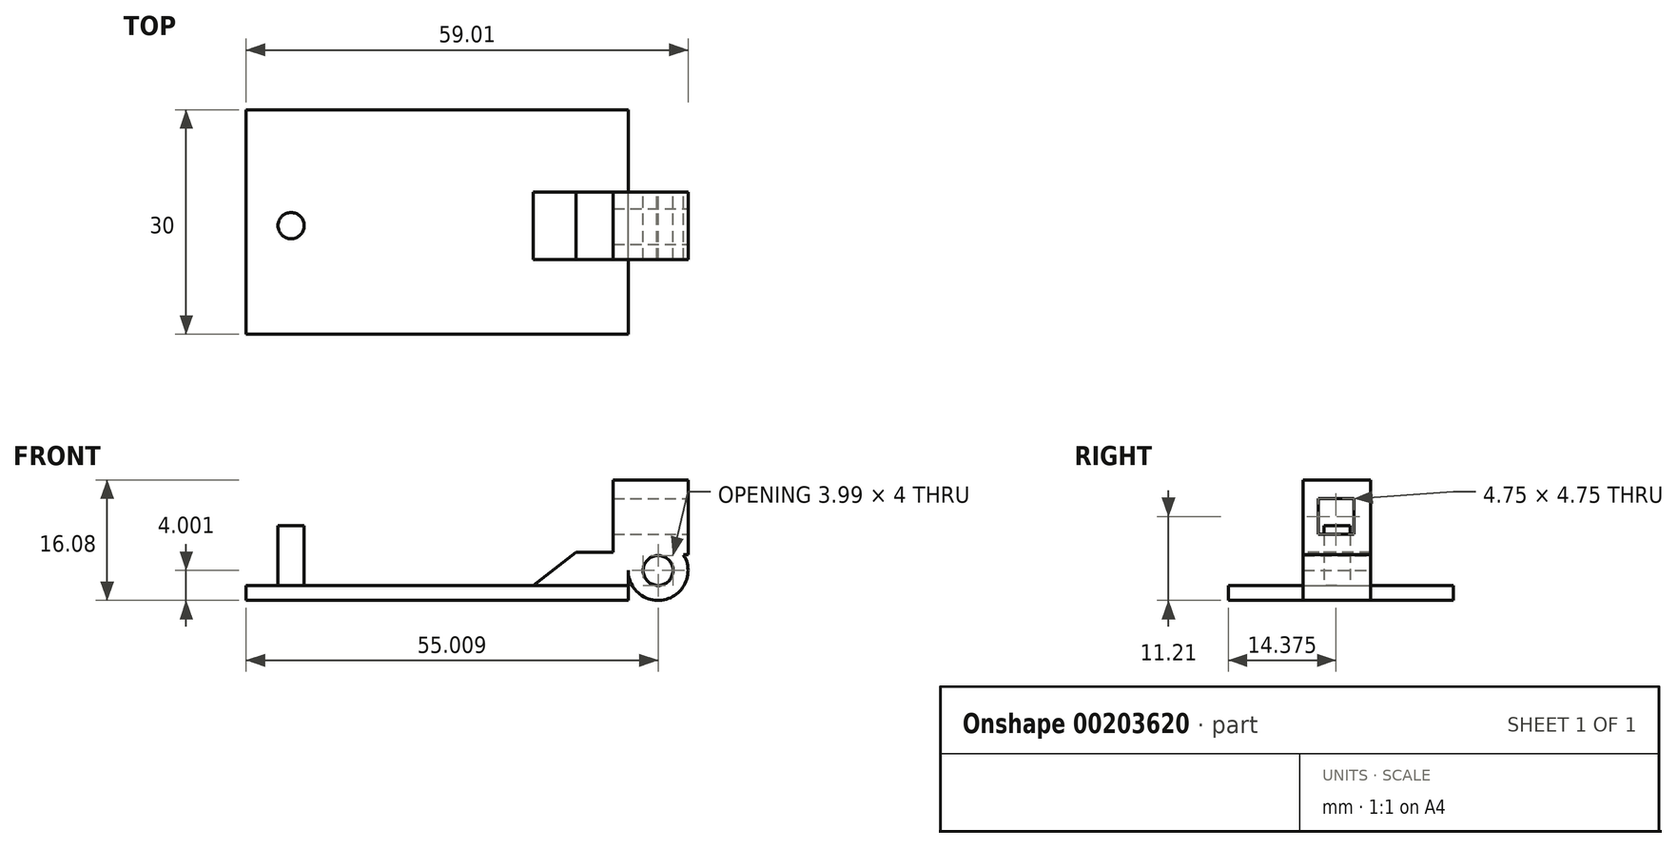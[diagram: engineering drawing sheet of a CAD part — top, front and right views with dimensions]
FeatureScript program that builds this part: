
annotation { "Feature Type Name" : "Feature", "Feature Type Description" : "" }
export const myFeature = defineFeature(function(context is Context, id is Id, definition is map)
    precondition{}
    {
        {
            var Q0;
            Q0=qCreatedBy(makeId("Front.planeOp"),FACE);
            var sketch = newSketch(context, id + "F0", { "sketchPlane" : qUnion([Q0])});
            skLineSegment(sketch, "E0.bottom", {"start": v(0, -4) * mm, "end": v(55, -4) * mm});
            skLineSegment(sketch, "E0.top", {"start": v(0, -2) * mm, "end": v(55, -2) * mm});
            skLineSegment(sketch, "E0.left", {"start": v(0, -4) * mm, "end": v(0, -2) * mm});
            skLineSegment(sketch, "E0.right", {"start": v(55, -4) * mm, "end": v(55, -2) * mm});
            skLineSegment(sketch, "E1", {"start": v(55, -2) * mm, "end": v(55, 0) * mm});
            skCircle(sketch, "E2", {"center": v(55, 0) * mm, "radius": 4 * mm});
            skCircle(sketch, "E3", {"center": v(55, 0) * mm, "radius": 2 * mm});
            skLineSegment(sketch, "E4", {"start": v(51, 0) * mm, "end": v(51, -4) * mm});
            skLineSegment(sketch, "E5", {"start": v(51.84, 2.44) * mm, "end": v(44.02, 2.44) * mm});
            skLineSegment(sketch, "E6", {"start": v(44.02, 2.44) * mm, "end": v(38.32, -2) * mm});
            skSolve(sketch);
        }
        {
            var Q0;
            {var subQ1=sQuery(id+"F0.wireOp",EDGE,"msGZdTGy-w9Bb-bp7U-2m3c-FxzwhI83p8LT");var subQ3=sQuery(id+"F0.wireOp",EDGE,"E0.top");var subQ4=makeQuery(id+"F0.imprint","INTERSECT",VERTEX,{"derivedFrom":[subQ1,subQ3]});Q0=makeQuery(id+"F0.imprint","IMPRINT",FACE,{"disambiguationData":[TD([[makeQuery(id+"F0.imprint","IMPRINT",EDGE,{"disambiguationData":[TD([[subQ4,-1.0]])],"derivedFrom":subQ3}),-1.0]])]});}
            var Q1;
            {var subQ0=sQuery(id+"F0.wireOp",EDGE,"E0.left");Q1=makeQuery(id+"F0.imprint","IMPRINT",FACE,{"disambiguationData":[TD([[makeQuery(id+"F0.imprint","IMPRINT",EDGE,{"derivedFrom":subQ0}),-1.0]])]});}
            var Q2;
            {var subQ0=sQuery(id+"F0.wireOp",EDGE,"E0.right");Q2=makeQuery(id+"F0.imprint","IMPRINT",FACE,{"disambiguationData":[TD([[makeQuery(id+"F0.imprint","IMPRINT",EDGE,{"derivedFrom":subQ0}),1.0]])]});}
            var Q3;
            {var subQ4=sQuery(id+"F0.wireOp",EDGE,"E0.right");var subQ5=sQuery(id+"F0.wireOp",EDGE,"E0.bottom");var subQ6=makeQuery(id+"F0.imprint","INTERSECT",VERTEX,{"derivedFrom":[subQ5,subQ4]});Q3=makeQuery(id+"F0.imprint","IMPRINT",FACE,{"disambiguationData":[TD([[makeQuery(id+"F0.imprint","IMPRINT",EDGE,{"disambiguationData":[TD([[subQ6,1.0]])],"derivedFrom":subQ5}),-1.0]])]});}
            var Q4;
            {var subQ1=sQuery(id+"F0.wireOp",EDGE,"E0.bottom");var subQ5=sQuery(id+"F0.wireOp",EDGE,"E0.right");var subQ6=makeQuery(id+"F0.imprint","INTERSECT",VERTEX,{"derivedFrom":[subQ1,subQ5]});Q4=makeQuery(id+"F0.imprint","IMPRINT",FACE,{"disambiguationData":[TD([[makeQuery(id+"F0.imprint","IMPRINT",EDGE,{"disambiguationData":[TD([[subQ6,1.0]])],"derivedFrom":subQ1}),1.0]])]});}
            var Q5;
            {var subQ6=sQuery(id+"F0.wireOp",EDGE,"E5");Q5=makeQuery(id+"F0.imprint","IMPRINT",FACE,{"disambiguationData":[TD([[makeQuery(id+"F0.imprint","IMPRINT",EDGE,{"derivedFrom":subQ6}),1.0]])]});}
            extrude(context, id + "F1", {"entities" : qUnion([Q0, Q1, Q2, Q3, Q4, Q5]), "depth" : 20 * mm, "hasSecondDirection" : true, "secondDirectionOppositeDirection" : false, "secondDirectionDepth" : 11 * mm});
        }
        {
            var Q0;
            {var subQ0=sQuery(id+"F0.wireOp",EDGE,"E0.bottom");Q0=makeQuery(id+"F0amyIbCvxJC7EA_1.boolean.opBoolean","MERGE",FACE,{"derivedFrom":[makeQuery(id+"FixQ7C7vZYy5nc9_1.boolean.opBoolean","MERGE",FACE,{"derivedFrom":[makeQuery(id+"F1.opExtrude","SWEPT_FACE",FACE,{"disambiguationData":[OSD([subQ0])]}),makeQuery(id+"FixQ7C7vZYy5nc9_1.opExtrude","SWEPT_FACE",FACE,{"disambiguationData":[OSD([subQ0])]})]}),makeQuery(id+"F0amyIbCvxJC7EA_1.opExtrude","SWEPT_FACE",FACE,{"disambiguationData":[OSD([subQ0])]})]});}
            var sketch = newSketch(context, id + "F2", { "sketchPlane" : qUnion([Q0])});
            skLineSegment(sketch, "E7", {"start": v(6, 20) * mm, "end": v(6, 15.5) * mm});
            skCircle(sketch, "E8", {"center": v(6, 15.5) * mm, "radius": 1.75 * mm});
            skSolve(sketch);
        }
        {
            var Q0;
            Q0=makeQuery(id+"F1.opExtrude","SWEPT_FACE",FACE,{"disambiguationData":[OSD([sQuery(id+"F0.wireOp",EDGE,"E4")])]});
            var sketch = newSketch(context, id + "F3", { "sketchPlane" : qUnion([Q0])});
            skLineSegment(sketch, "E9", {"start": v(-20, 2.07) * mm, "end": v(-20, 12.07) * mm});
            skLineSegment(sketch, "E10", {"start": v(-20, 12.07) * mm, "end": v(-11, 12.07) * mm});
            skLineSegment(sketch, "E11.bottom", {"start": v(-18, 9.57) * mm, "end": v(-13.25, 9.57) * mm});
            skLineSegment(sketch, "E11.top", {"start": v(-18, 4.82) * mm, "end": v(-13.25, 4.82) * mm});
            skLineSegment(sketch, "E11.left", {"start": v(-18, 9.57) * mm, "end": v(-18, 4.82) * mm});
            skLineSegment(sketch, "E11.right", {"start": v(-13.25, 9.57) * mm, "end": v(-13.25, 4.82) * mm});
            skLineSegment(sketch, "E12", {"start": v(-20, 2.07) * mm, "end": v(-11, 2.07) * mm});
            skLineSegment(sketch, "E13", {"start": v(-11, 12.07) * mm, "end": v(-11, 2.07) * mm});
            skLineSegment(sketch, "E14", {"start": v(-20, 2.07) * mm, "end": v(-20, -4) * mm});
            skLineSegment(sketch, "E15", {"start": v(-20, -4) * mm, "end": v(-11, -4) * mm});
            skLineSegment(sketch, "E16", {"start": v(-11, -4) * mm, "end": v(-11, 2.07) * mm});
            skLineSegment(sketch, "E17", {"start": v(-13.25, 9.57) * mm, "end": v(-8.24, 9.57) * mm});
            skSolve(sketch);
        }
        {
            var Q0;
            Q0=makeQuery(id+"F3.imprint","IMPRINT",FACE,{"disambiguationData":[TD([[makeQuery(id+"F3.imprint","IMPRINT",EDGE,{"derivedFrom":sQuery(id+"F3.wireOp",EDGE,"E9")}),-1.0]])]});
            extrude(context, id + "F4", {"entities" : qUnion([Q0]), "operationType" : NewBodyOperationType.ADD, "oppositeDirection" : true, "depth" : 2 * mm, "hasSecondDirection" : true, "secondDirectionOppositeDirection" : false, "secondDirectionDepth" : 8 * mm});
        }
        {
            var Q0;
            {var subQ0=sQuery(id+"F3.wireOp",EDGE,"E12");Q0=makeQuery(id+"F3.imprint","IMPRINT",FACE,{"disambiguationData":[TD([[makeQuery(id+"F3.imprint","IMPRINT",EDGE,{"derivedFrom":subQ0}),-1.0]])]});}
            extrude(context, id + "F5", {"entities" : qUnion([Q0]), "operationType" : NewBodyOperationType.ADD, "oppositeDirection" : true, "depth" : 6 * mm, "hasSecondDirection" : true, "secondDirectionOppositeDirection" : false, "secondDirectionDepth" : 2 * mm});
        }
        {
            var Q0;
            {var subQ0=sQuery(id+"F0.wireOp",EDGE,"E0.left");Q0=makeQuery(id+"F0.imprint","IMPRINT",FACE,{"disambiguationData":[TD([[makeQuery(id+"F0.imprint","IMPRINT",EDGE,{"derivedFrom":subQ0}),-1.0]])]});}
            extrude(context, id + "F6", {"entities" : qUnion([Q0]), "operationType" : NewBodyOperationType.ADD, "depth" : 30 * mm});
        }
        {
            var Q0;
            Q0=makeQuery(id+"F2.imprint","IMPRINT",FACE,{"disambiguationData":[TD([[makeQuery(id+"F2.imprint","IMPRINT",EDGE,{"derivedFrom":sQuery(id+"F2.wireOp",EDGE,"E8")}),1.0]])]});
            extrude(context, id + "F7", {"entities" : qUnion([Q0]), "operationType" : NewBodyOperationType.ADD, "oppositeDirection" : true, "depth" : 10 * mm});
        }
    });
